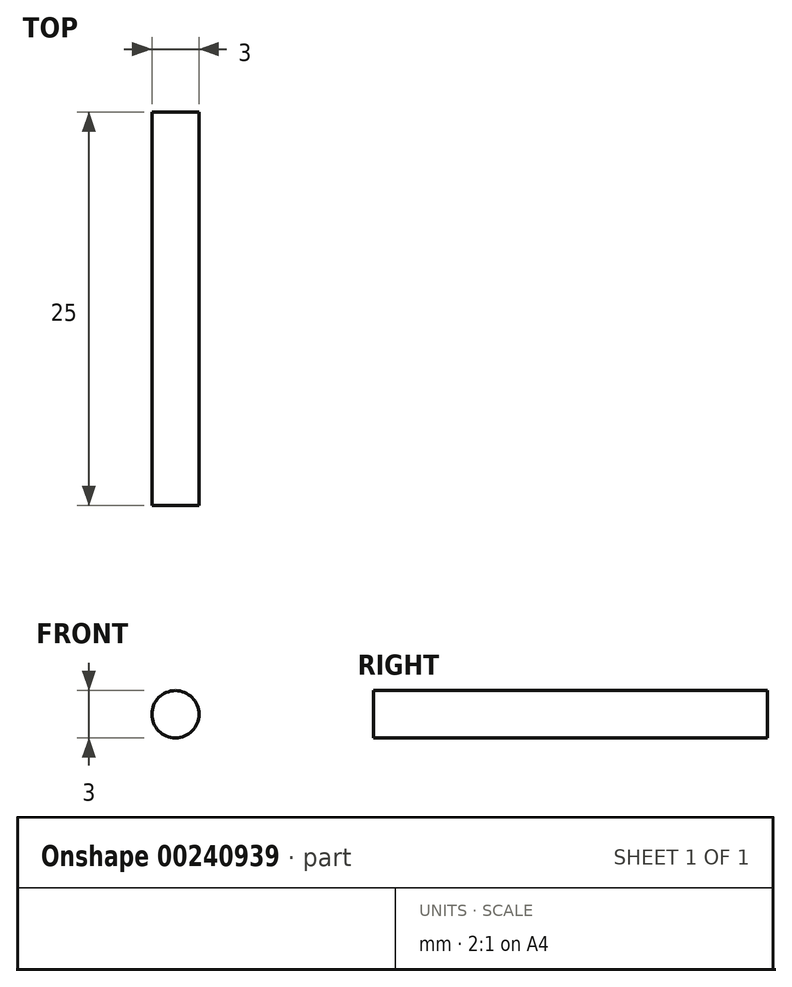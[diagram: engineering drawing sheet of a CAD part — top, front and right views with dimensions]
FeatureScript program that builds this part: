
annotation { "Feature Type Name" : "Feature", "Feature Type Description" : "" }
export const myFeature = defineFeature(function(context is Context, id is Id, definition is map)
    precondition{}
    {
        {
            var Q0;
            Q0=qCreatedBy(makeId("Front.planeOp"),FACE);
            var sketch = newSketch(context, id + "F0", { "sketchPlane" : qUnion([Q0])});
            skCircle(sketch, "E0", {"center": v(0, 0) * mm, "radius": 1.5 * mm});
            skSolve(sketch);
        }
        {
            var Q0;
            Q0=makeQuery(id+"F0.imprint","IMPRINT",FACE,{"disambiguationData":[TD([[makeQuery(id+"F0.imprint","IMPRINT",EDGE,{"derivedFrom":sQuery(id+"F0.wireOp",EDGE,"E0")}),1.0]])]});
            extrude(context, id + "F1", {"entities" : qUnion([Q0]), "depth" : 25 * mm});
        }
    });
